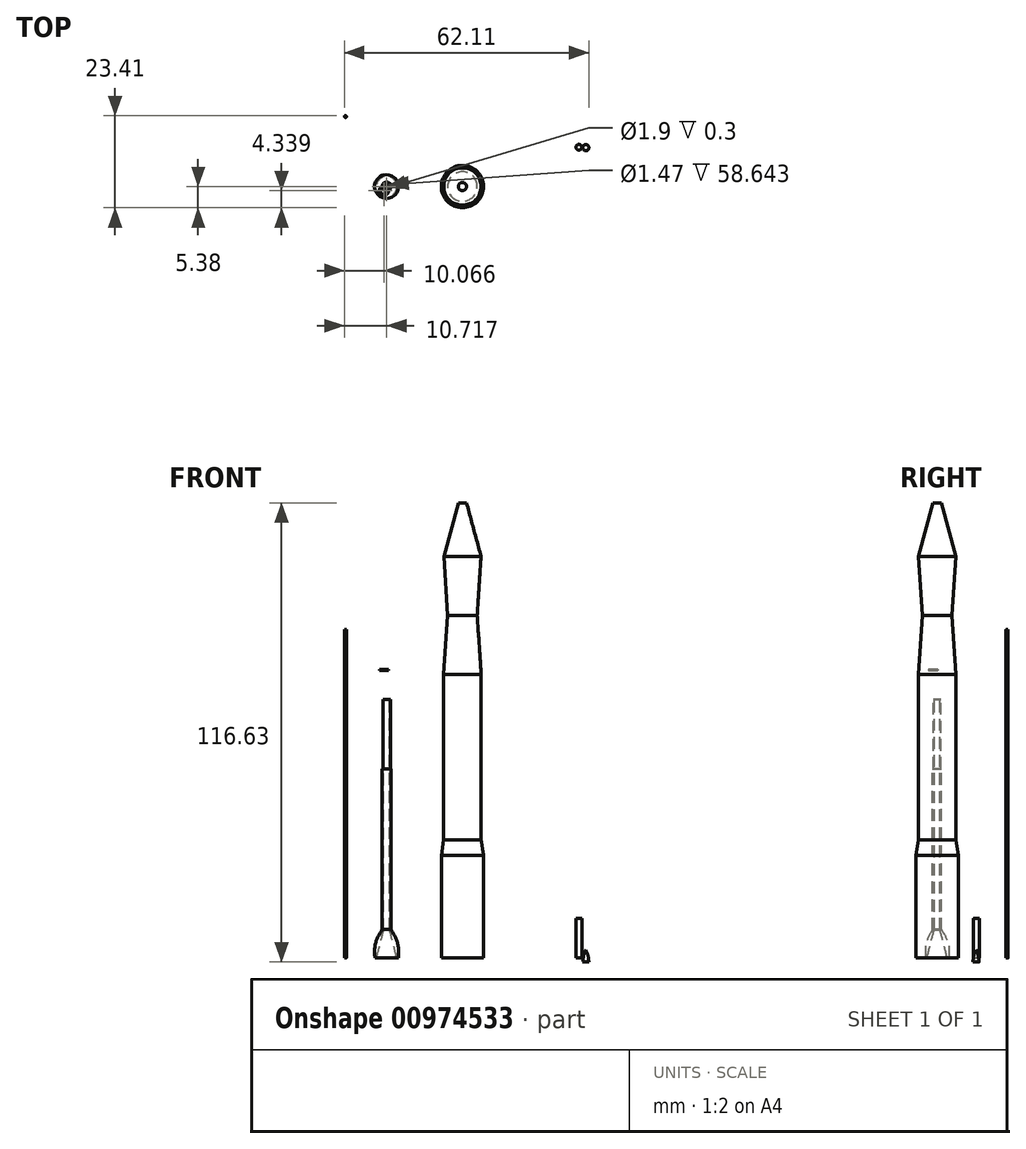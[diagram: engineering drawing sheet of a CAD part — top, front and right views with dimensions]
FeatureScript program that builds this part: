
annotation { "Feature Type Name" : "Feature", "Feature Type Description" : "" }
export const myFeature = defineFeature(function(context is Context, id is Id, definition is map)
    precondition{}
    {
        {
            var Q0;
            Q0=qCreatedBy(makeId("Top.planeOp"),FACE);
            var sketch = newSketch(context, id + "F0", { "sketchPlane" : qUnion([Q0])});
            skCircle(sketch, "E0", {"center": v(0, 0) * mm, "radius": 5.38 * mm});
            skSolve(sketch);
        }
        {
            var Q0;
            Q0=makeQuery(id+"F0.imprint","IMPRINT",FACE,{"disambiguationData":[TD([[makeQuery(id+"F0.imprint","IMPRINT",EDGE,{"derivedFrom":sQuery(id+"F0.wireOp",EDGE,"E0")}),1.0]])]});
            cPlane(context, id + "F1", {"entities" : qUnion([Q0]), "cplaneType" : CPlaneType.OFFSET, "offset" : 26 * mm, "width" : 150 * mm, "height" : 150 * mm});
        }
        {
            var Q0;
            Q0=qCreatedBy(id+"F1.planeOp",FACE);
            var sketch = newSketch(context, id + "F2", { "sketchPlane" : qUnion([Q0])});
            skCircle(sketch, "E1", {"center": v(0, 0) * mm, "radius": 5.38 * mm});
            skSolve(sketch);
        }
        {
            var Q0;
            Q0=makeQuery(id+"F2.imprint","IMPRINT",FACE,{"disambiguationData":[TD([[makeQuery(id+"F2.imprint","IMPRINT",EDGE,{"derivedFrom":sQuery(id+"F2.wireOp",EDGE,"E1")}),1.0]])]});
            cPlane(context, id + "F3", {"entities" : qUnion([Q0]), "cplaneType" : CPlaneType.OFFSET, "offset" : 4 * mm, "width" : 150 * mm, "height" : 150 * mm});
        }
        {
            var Q0;
            Q0=qCreatedBy(id+"F3.planeOp",FACE);
            var sketch = newSketch(context, id + "F4", { "sketchPlane" : qUnion([Q0])});
            skCircle(sketch, "E2", {"center": v(0, 0) * mm, "radius": 4.75 * mm});
            skSolve(sketch);
        }
        {
            var Q0;
            Q0=makeQuery(id+"F4.imprint","IMPRINT",FACE,{"disambiguationData":[TD([[makeQuery(id+"F4.imprint","IMPRINT",EDGE,{"derivedFrom":sQuery(id+"F4.wireOp",EDGE,"E2")}),1.0]])]});
            cPlane(context, id + "F5", {"entities" : qUnion([Q0]), "cplaneType" : CPlaneType.OFFSET, "offset" : 42 * mm, "width" : 150 * mm, "height" : 150 * mm});
        }
        {
            var Q0;
            Q0=qCreatedBy(id+"F5.planeOp",FACE);
            var sketch = newSketch(context, id + "F6", { "sketchPlane" : qUnion([Q0])});
            skCircle(sketch, "E3", {"center": v(0, 0) * mm, "radius": 4.78 * mm});
            skSolve(sketch);
        }
        {
            var Q0;
            Q0=makeQuery(id+"F4.imprint","IMPRINT",FACE,{"disambiguationData":[TD([[makeQuery(id+"F4.imprint","IMPRINT",EDGE,{"derivedFrom":sQuery(id+"F4.wireOp",EDGE,"E2")}),1.0]])]});
            extrude(context, id + "F7", {"entities" : qUnion([Q0]), "depth" : 42 * mm, "offsetDistance" : 25 * mm});
        }
        {
            var Q0;
            Q0=makeQuery(id+"F0.imprint","IMPRINT",FACE,{"disambiguationData":[TD([[makeQuery(id+"F0.imprint","IMPRINT",EDGE,{"derivedFrom":sQuery(id+"F0.wireOp",EDGE,"E0")}),1.0]])]});
            extrude(context, id + "F8", {"entities" : qUnion([Q0]), "depth" : 26 * mm, "offsetDistance" : 25 * mm});
        }
        {
            var Q0;
            Q0=makeQuery(id+"F2.imprint","IMPRINT",FACE,{"disambiguationData":[TD([[makeQuery(id+"F2.imprint","IMPRINT",EDGE,{"derivedFrom":sQuery(id+"F2.wireOp",EDGE,"E1")}),1.0]])]});
            var Q1;
            Q1=makeQuery(id+"F7.opExtrude","CAP_FACE",FACE,{"disambiguationData":[OSD([sQuery(id+"F4.wireOp",EDGE,"E2")])],"isStart":true});
            loft(context, id + "F9", {"sheetProfilesArray" : [{ "sheetProfileEntities" : qUnion([Q0]) }, { "sheetProfileEntities" : qUnion([Q1]) }]});
        }
        {
            var Q0;
            Q0=makeQuery(id+"F6.imprint","IMPRINT",FACE,{"disambiguationData":[TD([[makeQuery(id+"F6.imprint","IMPRINT",EDGE,{"derivedFrom":sQuery(id+"F6.wireOp",EDGE,"E3")}),1.0]])]});
            cPlane(context, id + "F10", {"entities" : qUnion([Q0]), "cplaneType" : CPlaneType.OFFSET, "offset" : 15 * mm, "width" : 150 * mm, "height" : 150 * mm});
        }
        {
            var Q0;
            Q0=qCreatedBy(id+"F10.planeOp",FACE);
            var sketch = newSketch(context, id + "F11", { "sketchPlane" : qUnion([Q0])});
            skCircle(sketch, "E4", {"center": v(0, 0) * mm, "radius": 3.75 * mm});
            skSolve(sketch);
        }
        {
            var Q1;
            Q1=makeQuery(id+"F6.imprint","IMPRINT",FACE,{"disambiguationData":[TD([[makeQuery(id+"F6.imprint","IMPRINT",EDGE,{"derivedFrom":sQuery(id+"F6.wireOp",EDGE,"E3")}),1.0]])]});
            var Q2;
            Q2=makeQuery(id+"F11.imprint","IMPRINT",FACE,{"disambiguationData":[TD([[makeQuery(id+"F11.imprint","IMPRINT",EDGE,{"derivedFrom":sQuery(id+"F11.wireOp",EDGE,"E4")}),1.0]])]});
            loft(context, id + "F12", {"operationType" : NewBodyOperationType.ADD, "sheetProfilesArray" : [{ "sheetProfileEntities" : qUnion([Q1]) }, { "sheetProfileEntities" : qUnion([Q2]) }]});
        }
        {
            var Q0;
            Q0=qCreatedBy(id+"F10.planeOp",FACE);
            cPlane(context, id + "F13", {"entities" : qUnion([Q0]), "cplaneType" : CPlaneType.OFFSET, "offset" : 15 * mm, "width" : 150 * mm, "height" : 150 * mm});
        }
        {
            var Q0;
            Q0=qCreatedBy(id+"F13.planeOp",FACE);
            var sketch = newSketch(context, id + "F14", { "sketchPlane" : qUnion([Q0])});
            skCircle(sketch, "E5", {"center": v(0, 0) * mm, "radius": 4.74 * mm});
            skSolve(sketch);
        }
        {
            var Q1;
            Q1=makeQuery(id+"F12.opLoft","CAP_FACE",FACE,{"disambiguationData":[OSD([makeQuery(id+"F11.imprint","IMPRINT",FACE,{"disambiguationData":[TD([[makeQuery(id+"F11.imprint","IMPRINT",EDGE,{"derivedFrom":sQuery(id+"F11.wireOp",EDGE,"E4")}),1.0]])]})])],"isStart":true});
            var Q2;
            Q2=makeQuery(id+"F14.imprint","IMPRINT",FACE,{"disambiguationData":[TD([[makeQuery(id+"F14.imprint","IMPRINT",EDGE,{"derivedFrom":sQuery(id+"F14.wireOp",EDGE,"E5")}),1.0]])]});
            loft(context, id + "F15", {"operationType" : NewBodyOperationType.ADD, "sheetProfilesArray" : [{ "sheetProfileEntities" : qUnion([Q1]) }, { "sheetProfileEntities" : qUnion([Q2]) }]});
        }
        {
            var Q0;
            Q0=qCreatedBy(makeId("Top.planeOp"),FACE);
            var sketch = newSketch(context, id + "F16", { "sketchPlane" : qUnion([Q0])});
            skCircle(sketch, "E6", {"center": v(-21.4, 0) * mm, "radius": 3.3 * mm});
            skSolve(sketch);
        }
        {
            var Q0;
            Q0=makeQuery(id+"F16.imprint","IMPRINT",FACE,{"disambiguationData":[TD([[makeQuery(id+"F16.imprint","IMPRINT",EDGE,{"derivedFrom":sQuery(id+"F16.wireOp",EDGE,"E6")}),1.0]])]});
            cPlane(context, id + "F17", {"entities" : qUnion([Q0]), "cplaneType" : CPlaneType.OFFSET, "offset" : 4 * mm, "width" : 150 * mm, "height" : 150 * mm});
        }
        {
            var Q0;
            Q0=makeQuery(id+"F16.imprint","IMPRINT",FACE,{"disambiguationData":[TD([[makeQuery(id+"F16.imprint","IMPRINT",EDGE,{"derivedFrom":sQuery(id+"F16.wireOp",EDGE,"E6")}),1.0]])]});
            cPlane(context, id + "F18", {"entities" : qUnion([Q0]), "cplaneType" : CPlaneType.OFFSET, "offset" : 8 * mm, "width" : 150 * mm, "height" : 150 * mm});
        }
        {
            var Q0;
            Q0=qCreatedBy(id+"F17.planeOp",FACE);
            var sketch = newSketch(context, id + "F19", { "sketchPlane" : qUnion([Q0])});
            skCircle(sketch, "E7", {"center": v(-21.4, 0) * mm, "radius": 3.15 * mm});
            skSolve(sketch);
        }
        {
            var Q0;
            Q0=qCreatedBy(id+"F18.planeOp",FACE);
            var sketch = newSketch(context, id + "F20", { "sketchPlane" : qUnion([Q0])});
            skCircle(sketch, "E8", {"center": v(-21.4, 0) * mm, "radius": 1.25 * mm});
            skSolve(sketch);
        }
        {
            var Q0;
            Q0=makeQuery(id+"F20.imprint","IMPRINT",FACE,{"disambiguationData":[TD([[makeQuery(id+"F20.imprint","IMPRINT",EDGE,{"derivedFrom":sQuery(id+"F20.wireOp",EDGE,"E8")}),1.0]])]});
            cPlane(context, id + "F21", {"entities" : qUnion([Q0]), "cplaneType" : CPlaneType.OFFSET, "offset" : 65 * mm, "width" : 150 * mm, "height" : 150 * mm});
        }
        {
            var Q0;
            Q0=qCreatedBy(id+"F21.planeOp",FACE);
            var sketch = newSketch(context, id + "F22", { "sketchPlane" : qUnion([Q0])});
            skCircle(sketch, "E9", {"center": v(-21.4, 0) * mm, "radius": 1.26 * mm});
            skSolve(sketch);
        }
        {
            var Q0;
            Q0=makeQuery(id+"F16.imprint","IMPRINT",FACE,{"disambiguationData":[TD([[makeQuery(id+"F16.imprint","IMPRINT",EDGE,{"derivedFrom":sQuery(id+"F16.wireOp",EDGE,"E6")}),1.0]])]});
            var Q1;
            Q1=makeQuery(id+"F19.imprint","IMPRINT",FACE,{"disambiguationData":[TD([[makeQuery(id+"F19.imprint","IMPRINT",EDGE,{"derivedFrom":sQuery(id+"F19.wireOp",EDGE,"E7")}),1.0]])]});
            var Q2;
            Q2=makeQuery(id+"F20.imprint","IMPRINT",FACE,{"disambiguationData":[TD([[makeQuery(id+"F20.imprint","IMPRINT",EDGE,{"derivedFrom":sQuery(id+"F20.wireOp",EDGE,"E8")}),1.0]])]});
            loft(context, id + "F23", {"sheetProfilesArray" : [{ "sheetProfileEntities" : qUnion([Q0]) }, { "sheetProfileEntities" : qUnion([Q1]) }, { "sheetProfileEntities" : qUnion([Q2]) }]});
        }
        {
            var Q0;
            Q0=makeQuery(id+"F22.imprint","IMPRINT",FACE,{"disambiguationData":[TD([[makeQuery(id+"F22.imprint","IMPRINT",EDGE,{"derivedFrom":sQuery(id+"F22.wireOp",EDGE,"E9")}),1.0]])]});
            var Q1;
            Q1=makeQuery(id+"F23.opLoft","CAP_FACE",FACE,{"disambiguationData":[OSD([makeQuery(id+"F20.imprint","IMPRINT",FACE,{"disambiguationData":[TD([[makeQuery(id+"F20.imprint","IMPRINT",EDGE,{"derivedFrom":sQuery(id+"F20.wireOp",EDGE,"E8")}),1.0]])]})])],"isStart":true});
            extrude(context, id + "F24", {"entities" : qUnion([Q0]), "operationType" : NewBodyOperationType.ADD, "endBound" : BoundingType.UP_TO_SURFACE, "oppositeDirection" : true, "depth" : 25 * mm, "endBoundEntityFace" : qUnion([Q1]), "offsetDistance" : 25 * mm});
        }
        {
            var Q0;
            Q0=qCreatedBy(id+"F21.planeOp",FACE);
            var sketch = newSketch(context, id + "F25", { "sketchPlane" : qUnion([Q0])});
            skCircle(sketch, "E10", {"center": v(-21.4, 0) * mm, "radius": 0.82 * mm});
            skSolve(sketch);
        }
        {
            var Q0;
            Q0=qSketchRegion(id+"F25",true);
            extrude(context, id + "F26", {"entities" : qUnion([Q0]), "operationType" : NewBodyOperationType.REMOVE, "oppositeDirection" : true, "depth" : 1000 * mm, "offsetDistance" : 25 * mm});
        }
        {
            var Q0;
            Q0=qCreatedBy(makeId("Top.planeOp"),FACE);
            var sketch = newSketch(context, id + "F27", { "sketchPlane" : qUnion([Q0])});
            skCircle(sketch, "E11", {"center": v(-21.4, 0) * mm, "radius": 2.87 * mm});
            skSolve(sketch);
        }
        {
            var Q0;
            Q0=qCreatedBy(id+"F18.planeOp",FACE);
            var sketch = newSketch(context, id + "F28", { "sketchPlane" : qUnion([Q0])});
            skCircle(sketch, "E12", {"center": v(-21.38, 0) * mm, "radius": 0.8 * mm});
            skSolve(sketch);
        }
        {
            var Q1;
            Q1=qSketchRegion(id+"F27",true);
            var Q2;
            Q2=qSketchRegion(id+"F28",true);
            loft(context, id + "F29", {"operationType" : NewBodyOperationType.REMOVE, "sheetProfilesArray" : [{ "sheetProfileEntities" : qUnion([Q1]) }, { "sheetProfileEntities" : qUnion([Q2]) }]});
        }
        {
            var Q0;
            Q0=makeQuery(id+"F23.opLoft","SWEPT_BODY",BODY,{"disambiguationData":[OSD([makeQuery(id+"F16.imprint","IMPRINT",FACE,{"disambiguationData":[TD([[makeQuery(id+"F16.imprint","IMPRINT",EDGE,{"derivedFrom":sQuery(id+"F16.wireOp",EDGE,"E6")}),1.0]])]}),sQuery(id+"F19.wireOp",EDGE,"E7"),makeQuery(id+"F20.imprint","IMPRINT",FACE,{"disambiguationData":[TD([[makeQuery(id+"F20.imprint","IMPRINT",EDGE,{"derivedFrom":sQuery(id+"F20.wireOp",EDGE,"E8")}),1.0]])]})])]});
            var Q1;
            Q1=qCreatedBy(makeId("Origin.pointOp"),VERTEX);
            transform(context, id + "F30", {"entities" : qUnion([Q0]), "transformType" : TransformType.SCALE_UNIFORMLY, "scale" : .9, "scalePoint" : qUnion([Q1]), "makeCopy" : false});
        }
        {
            var Q0;
            Q0=qCreatedBy(id+"F21.planeOp",FACE);
            var sketch = newSketch(context, id + "F31", { "sketchPlane" : qUnion([Q0])});
            skCircle(sketch, "E13", {"center": v(-19.27, 0.01) * mm, "radius": 1.19 * mm});
            skCircle(sketch, "E14", {"center": v(-19.27, 0.01) * mm, "radius": 0.95 * mm});
            skSolve(sketch);
        }
        {
            var Q0;
            Q0=makeQuery(id+"F31.imprint","IMPRINT",FACE,{"disambiguationData":[TD([[makeQuery(id+"F31.imprint","IMPRINT",EDGE,{"derivedFrom":sQuery(id+"F31.wireOp",EDGE,"E13")}),1.0]])]});
            extrude(context, id + "F32", {"entities" : qUnion([Q0]), "operationType" : NewBodyOperationType.REMOVE, "oppositeDirection" : true, "depth" : 25 * mm, "offsetDistance" : 25 * mm});
        }
        {
            var Q0;
            Q0=qCreatedBy(id+"F21.planeOp",FACE);
            var sketch = newSketch(context, id + "F33", { "sketchPlane" : qUnion([Q0])});
            skCircle(sketch, "E15", {"center": v(-19.91, -1.04) * mm, "radius": 1.19 * mm});
            skCircle(sketch, "E16", {"center": v(-19.91, -1.04) * mm, "radius": 0.95 * mm});
            skSolve(sketch);
        }
        {
            var Q0;
            Q0=makeQuery(id+"F33.imprint","IMPRINT",FACE,{"disambiguationData":[TD([[makeQuery(id+"F33.imprint","IMPRINT",EDGE,{"derivedFrom":sQuery(id+"F33.wireOp",EDGE,"E15")}),1.0]])]});
            extrude(context, id + "F34", {"entities" : qUnion([Q0]), "depth" : .3 * mm, "offsetDistance" : 25 * mm});
        }
        {
            var Q0;
            Q0=qCreatedBy(makeId("Top.planeOp"),FACE);
            var sketch = newSketch(context, id + "F35", { "sketchPlane" : qUnion([Q0])});
            skCircle(sketch, "E17", {"center": v(-29.73, 17.78) * mm, "radius": 0.25 * mm});
            skSolve(sketch);
        }
        {
            var Q0;
            Q0=makeQuery(id+"F35.imprint","IMPRINT",FACE,{"disambiguationData":[TD([[makeQuery(id+"F35.imprint","IMPRINT",EDGE,{"derivedFrom":sQuery(id+"F35.wireOp",EDGE,"E17")}),1.0]])]});
            extrude(context, id + "F36", {"entities" : qUnion([Q0]), "depth" : 83.4 * mm, "offsetDistance" : 25 * mm});
        }
        {
            var Q0;
            Q0=makeQuery(id+"F15.opLoft","CAP_FACE",FACE,{"disambiguationData":[OSD([makeQuery(id+"F14.imprint","IMPRINT",FACE,{"disambiguationData":[TD([[makeQuery(id+"F14.imprint","IMPRINT",EDGE,{"derivedFrom":sQuery(id+"F14.wireOp",EDGE,"E5")}),1.0]])]})])],"isStart":true});
            cPlane(context, id + "F37", {"entities" : qUnion([Q0]), "cplaneType" : CPlaneType.OFFSET, "offset" : 13.6 * mm, "width" : 150 * mm, "height" : 150 * mm});
        }
        {
            var Q0;
            Q0=qCreatedBy(id+"F37.planeOp",FACE);
            var sketch = newSketch(context, id + "F38", { "sketchPlane" : qUnion([Q0])});
            skCircle(sketch, "E18", {"center": v(0, 0) * mm, "radius": 1.04 * mm});
            skSolve(sketch);
        }
        {
            var Q1;
            Q1=makeQuery(id+"F15.opLoft","CAP_FACE",FACE,{"disambiguationData":[OSD([makeQuery(id+"F14.imprint","IMPRINT",FACE,{"disambiguationData":[TD([[makeQuery(id+"F14.imprint","IMPRINT",EDGE,{"derivedFrom":sQuery(id+"F14.wireOp",EDGE,"E5")}),1.0]])]})])],"isStart":true});
            var Q2;
            Q2=makeQuery(id+"F38.imprint","IMPRINT",FACE,{"disambiguationData":[TD([[makeQuery(id+"F38.imprint","IMPRINT",EDGE,{"derivedFrom":sQuery(id+"F38.wireOp",EDGE,"E18")}),1.0]])]});
            loft(context, id + "F39", {"operationType" : NewBodyOperationType.ADD, "sheetProfilesArray" : [{ "sheetProfileEntities" : qUnion([Q1]) }, { "sheetProfileEntities" : qUnion([Q2]) }]});
        }
        {
            var Q0;
            Q0=qCreatedBy(makeId("Top.planeOp"),FACE);
            var sketch = newSketch(context, id + "F40", { "sketchPlane" : qUnion([Q0])});
            skCircle(sketch, "E19", {"center": v(29.59, 9.99) * mm, "radius": 0.74 * mm});
            skSolve(sketch);
        }
        {
            var Q0;
            Q0=makeQuery(id+"F40.imprint","IMPRINT",FACE,{"disambiguationData":[TD([[makeQuery(id+"F40.imprint","IMPRINT",EDGE,{"derivedFrom":sQuery(id+"F40.wireOp",EDGE,"E19")}),1.0]])]});
            var Q1;
            Q1=sQuery(id+"F40.wireOp",EDGE,"E19");
            extrude(context, id + "F41", {"entities" : qUnion([Q0]), "surfaceEntities" : qUnion([Q1]), "depth" : 10 * mm, "offsetDistance" : 25 * mm});
        }
        {
            var Q0;
            Q0=qCreatedBy(makeId("Top.planeOp"),FACE);
            var sketch = newSketch(context, id + "F42", { "sketchPlane" : qUnion([Q0])});
            skCircle(sketch, "E20", {"center": v(31.34, 9.88) * mm, "radius": 0.53 * mm});
            skSolve(sketch);
        }
        {
            var Q0;
            Q0=makeQuery(id+"F42.imprint","IMPRINT",FACE,{"disambiguationData":[TD([[makeQuery(id+"F42.imprint","IMPRINT",EDGE,{"derivedFrom":sQuery(id+"F42.wireOp",EDGE,"E20")}),1.0]])]});
            cPlane(context, id + "F43", {"entities" : qUnion([Q0]), "cplaneType" : CPlaneType.OFFSET, "offset" : 1.45 * mm, "width" : 150 * mm, "height" : 150 * mm});
        }
        {
            var Q0;
            Q0=qCreatedBy(id+"F43.planeOp",FACE);
            var sketch = newSketch(context, id + "F44", { "sketchPlane" : qUnion([Q0])});
            skCircle(sketch, "E21", {"center": v(31.34, 9.88) * mm, "radius": 0.26 * mm});
            skSolve(sketch);
        }
        {
            var Q0;
            Q0=makeQuery(id+"F44.imprint","IMPRINT",FACE,{"disambiguationData":[TD([[makeQuery(id+"F44.imprint","IMPRINT",EDGE,{"derivedFrom":sQuery(id+"F44.wireOp",EDGE,"E21")}),1.0]])]});
            cPlane(context, id + "F45", {"entities" : qUnion([Q0]), "cplaneType" : CPlaneType.OFFSET, "offset" : 0.6 * mm, "width" : 150 * mm, "height" : 150 * mm});
        }
        {
            var Q0;
            Q0=qCreatedBy(id+"F45.planeOp",FACE);
            var sketch = newSketch(context, id + "F46", { "sketchPlane" : qUnion([Q0])});
            skCircle(sketch, "E22", {"center": v(31.34, 9.88) * mm, "radius": 0.08 * mm});
            skSolve(sketch);
        }
        {
            var Q0;
            Q0=makeQuery(id+"F42.imprint","IMPRINT",FACE,{"disambiguationData":[TD([[makeQuery(id+"F42.imprint","IMPRINT",EDGE,{"derivedFrom":sQuery(id+"F42.wireOp",EDGE,"E20")}),1.0]])]});
            var Q1;
            Q1=makeQuery(id+"F44.imprint","IMPRINT",FACE,{"disambiguationData":[TD([[makeQuery(id+"F44.imprint","IMPRINT",EDGE,{"derivedFrom":sQuery(id+"F44.wireOp",EDGE,"E21")}),1.0]])]});
            var Q2;
            Q2=sQuery(id+"F46.wireOp",VERTEX,"E22.center");
            loft(context, id + "F47", {"sheetProfilesArray" : [{ "sheetProfileEntities" : qUnion([Q0]) }, { "sheetProfileEntities" : qUnion([Q1]) }, { "sheetProfileEntities" : qUnion([Q2]) }]});
        }
        {
            var Q0;
            Q0=makeQuery(id+"F47.opLoft","SWEPT_BODY",BODY,{"disambiguationData":[OSD([makeQuery(id+"F42.imprint","IMPRINT",FACE,{"disambiguationData":[TD([[makeQuery(id+"F42.imprint","IMPRINT",EDGE,{"derivedFrom":sQuery(id+"F42.wireOp",EDGE,"E20")}),1.0]])]}),sQuery(id+"F44.wireOp",EDGE,"E21"),sQuery(id+"F46.wireOp",VERTEX,"E22.center")])]});
            var Q1;
            Q1=qCreatedBy(id+"F47.opLoft",VERTEX);
            transform(context, id + "F48", {"entities" : qUnion([Q0]), "transformType" : TransformType.SCALE_UNIFORMLY, "scale" : 1.5, "scalePoint" : qUnion([Q1]), "makeCopy" : false});
        }
    });
